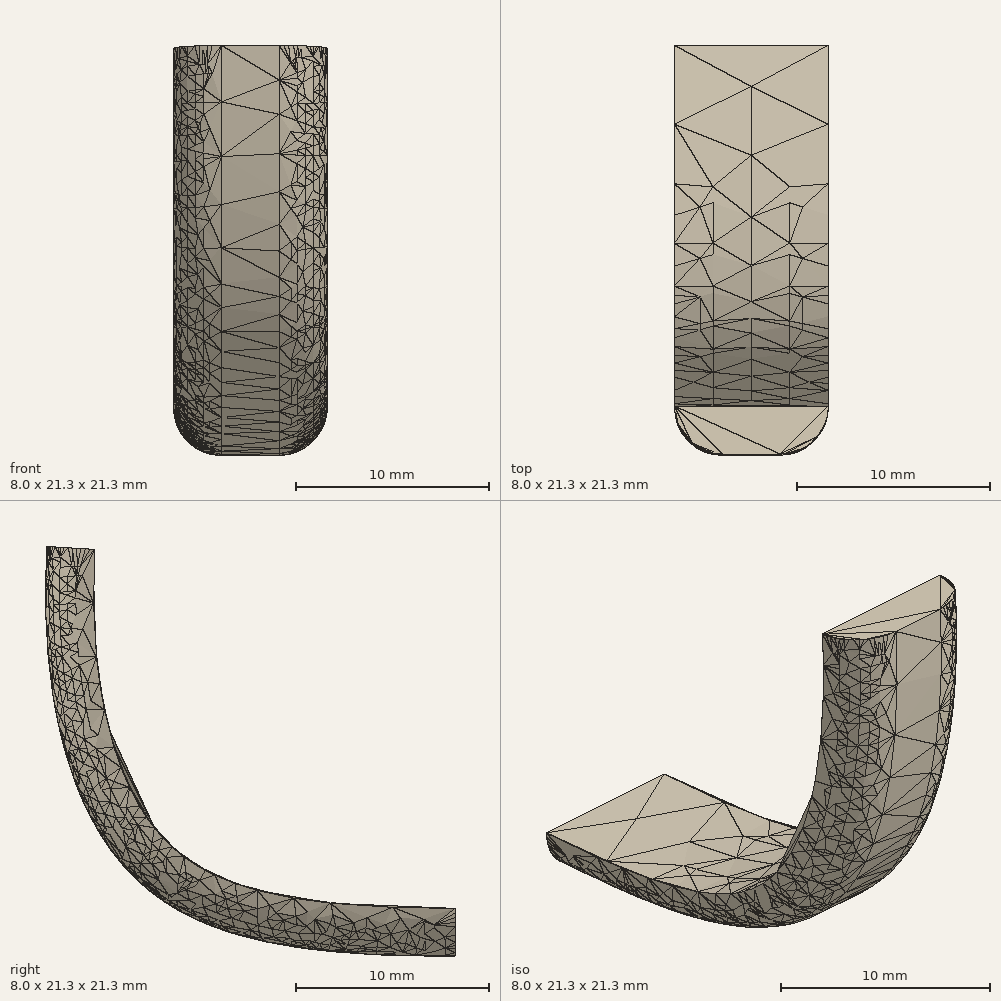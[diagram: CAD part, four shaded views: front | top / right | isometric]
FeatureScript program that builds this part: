
annotation { "Feature Type Name" : "Feature", "Feature Type Description" : "" }
export const myFeature = defineFeature(function(context is Context, id is Id, definition is map)
    precondition{}
    {
        {
            var Q0;
            Q0=qCreatedBy(makeId("Front.planeOp"),FACE);
            var sketch = newSketch(context, id + "F0", { "sketchPlane" : qUnion([Q0])});
            skLineSegment(sketch, "E0.bottom", {"start": v(4, -1.25) * mm, "end": v(-4, -1.25) * mm});
            skLineSegment(sketch, "E0.top", {"start": v(4, 1.25) * mm, "end": v(-4, 1.25) * mm});
            skLineSegment(sketch, "E0.left", {"start": v(4, -1.25) * mm, "end": v(4, 1.25) * mm});
            skLineSegment(sketch, "E0.right", {"start": v(-4, -1.25) * mm, "end": v(-4, 1.25) * mm});
            skPoint(sketch, "E0.middle", {"position": v(0, 0) * mm});
            skSolve(sketch);
        }
        {
            var Q0;
            Q0=qCreatedBy(makeId("Right.planeOp"),FACE);
            var sketch = newSketch(context, id + "F1", { "sketchPlane" : qUnion([Q0])});
            skFitSpline(sketch, "E1", {"points": [v(0, 0) * mm, v(-16.64, 4.67) * mm, v(-20, 20) * mm], "startDerivative": vector(-52.73, 0) * mm, "endDerivative": vector(2.27, 37.73) * mm});
            skSolve(sketch);
        }
        {
            var Q0;
            Q0=makeQuery(id+"F0.imprint","IMPRINT",FACE,{"disambiguationData":[TD([[makeQuery(id+"F0.imprint","IMPRINT",EDGE,{"derivedFrom":sQuery(id+"F0.wireOp",EDGE,"E0.bottom")}),-1.0]])]});
            var Q1;
            Q1=sQuery(id+"F1.wireOp",EDGE,"E1");
            sweep(context, id + "F2", {"profiles" : qUnion([Q0]), "path" : qUnion([Q1])});
        }
        {
            var Q0;
            Q0=makeQuery(id+"F2.opSweep","SWEPT_EDGE",EDGE,{"disambiguationData":[OSD([sQuery(id+"F0.wireOp",EDGE,"E0.bottom"),sQuery(id+"F0.wireOp",EDGE,"E0.left"),sQuery(id+"F1.wireOp",EDGE,"E1")])]});
            var Q1;
            Q1=makeQuery(id+"F2.opSweep","SWEPT_EDGE",EDGE,{"disambiguationData":[OSD([sQuery(id+"F0.wireOp",EDGE,"E0.bottom"),sQuery(id+"F0.wireOp",EDGE,"E0.right"),sQuery(id+"F1.wireOp",EDGE,"E1")])]});
            fillet(context, id + "F3", {"entities" : qUnion([Q0, Q1]), "radius" : 2.5 * mm, "tangentPropagation" : true, "allowEdgeOverflow" : false});
        }
    });
